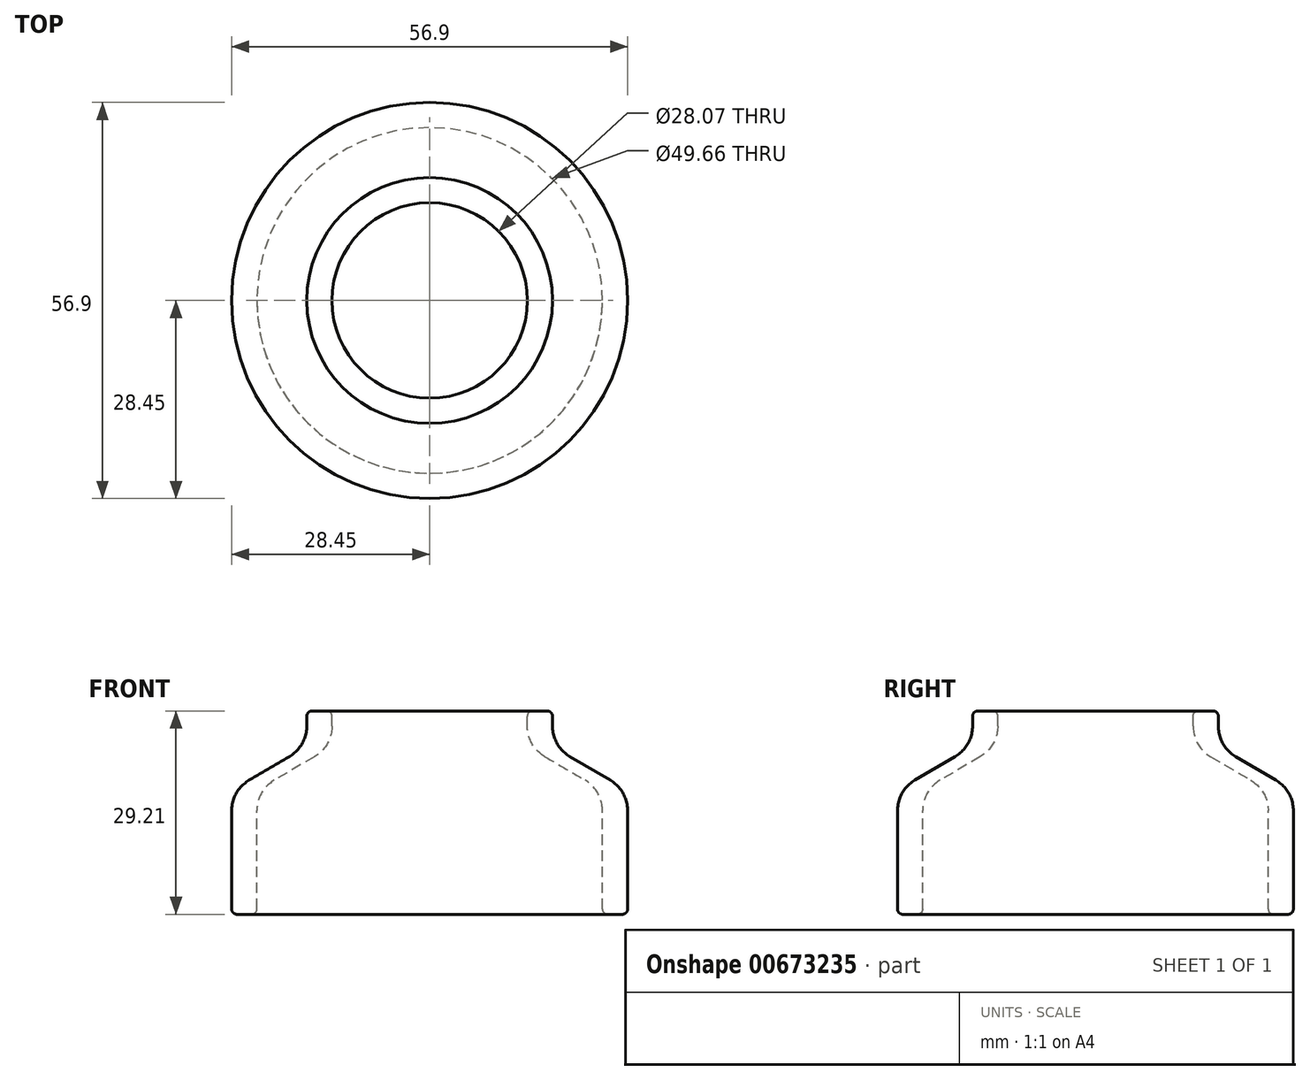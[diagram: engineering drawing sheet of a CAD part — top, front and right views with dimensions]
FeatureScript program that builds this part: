
annotation { "Feature Type Name" : "Feature", "Feature Type Description" : "" }
export const myFeature = defineFeature(function(context is Context, id is Id, definition is map)
    precondition{}
    {
        {
            var Q0;
            Q0=qCreatedBy(makeId("Front.planeOp"),FACE);
            var sketch = newSketch(context, id + "F0", { "sketchPlane" : qUnion([Q0])});
            skLineSegment(sketch, "E0", {"start": v(0, 5.93) * mm, "end": v(0, -7.11) * mm, "construction": true});
            skLineSegment(sketch, "E1", {"start": v(14.03, 29.21) * mm, "end": v(17.65, 29.21) * mm});
            skLineSegment(sketch, "E2", {"start": v(14.03, 29.21) * mm, "end": v(14.03, 24.13) * mm});
            skLineSegment(sketch, "E3", {"start": v(17.65, 29.21) * mm, "end": v(17.65, 24.13) * mm});
            skLineSegment(sketch, "E4", {"start": v(28.45, 0) * mm, "end": v(24.83, 0) * mm});
            skLineSegment(sketch, "E5", {"start": v(24.83, 0) * mm, "end": v(24.83, 17.78) * mm});
            skLineSegment(sketch, "E6", {"start": v(28.45, 0) * mm, "end": v(28.45, 17.78) * mm});
            skLineSegment(sketch, "E7", {"start": v(14.03, 24.13) * mm, "end": v(24.83, 17.78) * mm});
            skLineSegment(sketch, "E8", {"start": v(17.65, 24.13) * mm, "end": v(28.45, 17.78) * mm});
            skSolve(sketch);
        }
        {
            var Q0;
            Q0 = qSketchRegion(id + "F0", true);
            var Q1;
            Q1=sQuery(id+"F0.wireOp",EDGE,"E0");
            revolve(context, id + "F1", {"entities" : qUnion([Q0]), "axis" : qUnion([Q1]), "revolveType" : RevolveType.FULL});
        }
        {
            var Q0;
            Q0=makeQuery(id+"F1.opRevolve","SWEPT_EDGE",EDGE,{"disambiguationData":[OSD([sQuery(id+"F0.wireOp",EDGE,"E6"),sQuery(id+"F0.wireOp",EDGE,"E8")])]});
            var Q1;
            Q1=makeQuery(id+"F1.opRevolve","SWEPT_EDGE",EDGE,{"disambiguationData":[OSD([sQuery(id+"F0.wireOp",EDGE,"E3"),sQuery(id+"F0.wireOp",EDGE,"E8")])]});
            var Q2;
            Q2=makeQuery(id+"F1.opRevolve","SWEPT_EDGE",EDGE,{"disambiguationData":[OSD([sQuery(id+"F0.wireOp",EDGE,"E5"),sQuery(id+"F0.wireOp",EDGE,"E7")])]});
            var Q3;
            Q3=makeQuery(id+"F1.opRevolve","SWEPT_FACE",FACE,{"disambiguationData":[OSD([sQuery(id+"F0.wireOp",EDGE,"E7")])]});
            fillet(context, id + "F2", {"entities" : qUnion([Q0, Q1, Q2, Q3]), "radius" : 5.08 * mm, "tangentPropagation" : true, "allowEdgeOverflow" : false});
        }
        {
            var Q0;
            Q0=makeQuery(id+"F1.opRevolve","SWEPT_EDGE",EDGE,{"disambiguationData":[OSD([sQuery(id+"F0.wireOp",EDGE,"E1"),sQuery(id+"F0.wireOp",EDGE,"E3")])]});
            var Q1;
            Q1=makeQuery(id+"F1.opRevolve","SWEPT_EDGE",EDGE,{"disambiguationData":[OSD([sQuery(id+"F0.wireOp",EDGE,"E1"),sQuery(id+"F0.wireOp",EDGE,"E2")])]});
            var Q2;
            Q2=makeQuery(id+"F1.opRevolve","SWEPT_EDGE",EDGE,{"disambiguationData":[OSD([sQuery(id+"F0.wireOp",EDGE,"E4"),sQuery(id+"F0.wireOp",EDGE,"E6")])]});
            var Q3;
            Q3=makeQuery(id+"F1.opRevolve","SWEPT_EDGE",EDGE,{"disambiguationData":[OSD([sQuery(id+"F0.wireOp",EDGE,"E4"),sQuery(id+"F0.wireOp",EDGE,"E5")])]});
            fillet(context, id + "F3", {"entities" : qUnion([Q0, Q1, Q2, Q3]), "radius" : 0.76 * mm, "tangentPropagation" : true, "allowEdgeOverflow" : false});
        }
    });
